# Revit family: 2CKA006512A0334
name_source: partatom
category: Elektroinstallationen
revit_build: Autodesk Revit 2017 (Build: 20160225_1515(x64)
units: mm (PartAtom-declared; Revit-internal decimal feet)

## family parameters
Basisbauteil = Fläche
Beim Laden mit Abzugskörper schneiden = Nein
Bemaßung runder Anschluss = Durchmesser verwenden
Beschriftungsausrichtung beibehalten = Nein
Gemeinsam genutzt = Nein
Raumberechnungspunkt = Nein
Teiletyp = Normal

## types (1)
- 2CKA006512A0334
    Ausführung der Oberfläche = matt
    BIM = https://media.live.bim.site
    BIMSITE_PRODUCT_ID = 759cec85ea187d9e00c352de8b049e62ec88025f
    Bedienungsart = Dreh-/Druckknopf
    Befestigungsart = Krallen-/Schraubbefestigung
    Beschreibung = Busch-Drehdimmer, Busch-Dimmer, UP-Drehdimmer, Busch-Drehdimmer UP, LED, 2-100 W Mit Drehbetätigung, Druckfolgewechselschalter und Soft-Rastung. 2-Leiter-Anschlusstechnik (Neutralleiter nicht erforderlich). Optimiert für das Dimmen von Retrofit-LED-Leuchtmitteln (LEDi). Für dimmbare Retrofit-LED-Leuchtmittel (LEDi). Für dimmbare Retrofit-LED-Leuchtmittel (LEDi) an konventionellen oder elektronischen Transformatoren Für Glühlampen, 230 V-Halogenglühlampen, Niedervolt-Halogenlampen mit konventionellen oder elektronischen Transformatoren und dimmbare Halogen-Energiesparlampen. Mischlastbetrieb LEDi und herkömmliche Leuchtmittel möglich. Mittels Wahlschalter zwischen Phasenan- und Phasenabschnitt umschaltbar. Geräuscharm durch Einsatz von MOSFET-Transistoren. Kurzschlussfest und überlastsicher (elektronische Sicherung). Mit einstellbarer Minimalhelligkeit. Ohne Zentralscheibe. Nennspannung: 230 V~, + 10 % / - 10 % Nennfrequenz: 50 Hz/60 Hz Nennleistung: 2 - 100 W/VA (Retrofit-LED-Lasten). Nennleistung: 10 - 250 W/VA (Nicht-LED-Lasten). Schutzart Gerät: IP 20 Temperaturbereich Gerät: 0 °C bis 35 °C IEC 60669-2-1, British Standard EN 60669-2-1
    Datenblatt = https://media.live.bim.site
    Datenblatt 1 = https://media.live.bim.site U-102_CE_XX_V01_2CKA100000E1615.pdf
    Datenblatt 2 = https://media.live.bim.site
    Farbe = schwarz
    Frequenz [Hz] = [50:60]
    GTIN = 4011395212677
    Geeignet für Schutzart (IP) = IP20
    Gerätebreite [mm] = 71
    Gerätehöhe [mm] = 71
    Gerätetiefe [mm] = 32
    HAN = 2CKA006512A0334
    Halogenfrei = Ja
    HeinzeBIM = https://www.heinze.de
    Hersteller = Busch-Jaeger Elektro GmbH
    Ist System = Nein
    Ist Zubehör = Nein
    Lastart = universal und LED Retrofit
    Lichtwertspeicher = Ja
    Montageart = unter Putz
    Nebenstelleneingang = Ja
    Nennleistung [Voltampere] = [2:250]
    Nennspannung [Volt] = [207:253]
    Oberfläche = unbehandelt
    Produktseite = https://media.live.bim.site
    TYPE = 6523 U-102
    Typname = Busch-Drehdimmer, Busch-Dimmer, UP-Drehdimmer
    Verwendbar mit Bewegungsmelder = Nein
    Verwendbar mit IR-Taste = Nein
    Verwendbar mit Präsenzmelder = Nein
    Verwendbar mit Taste = Nein
    Verwendbar mit Zeitschalter/Timer = Nein
    Vorgabe-Ansicht = 1219 mm
    Werkstoff = Kunststoff
    Werkstoffgüte = Thermoplast
    White = White
    Zusammenstellung = Basiselement

## geometry (parser evidence)
native form markers: Sweep x3
no freeform markers — native parametric forms only
